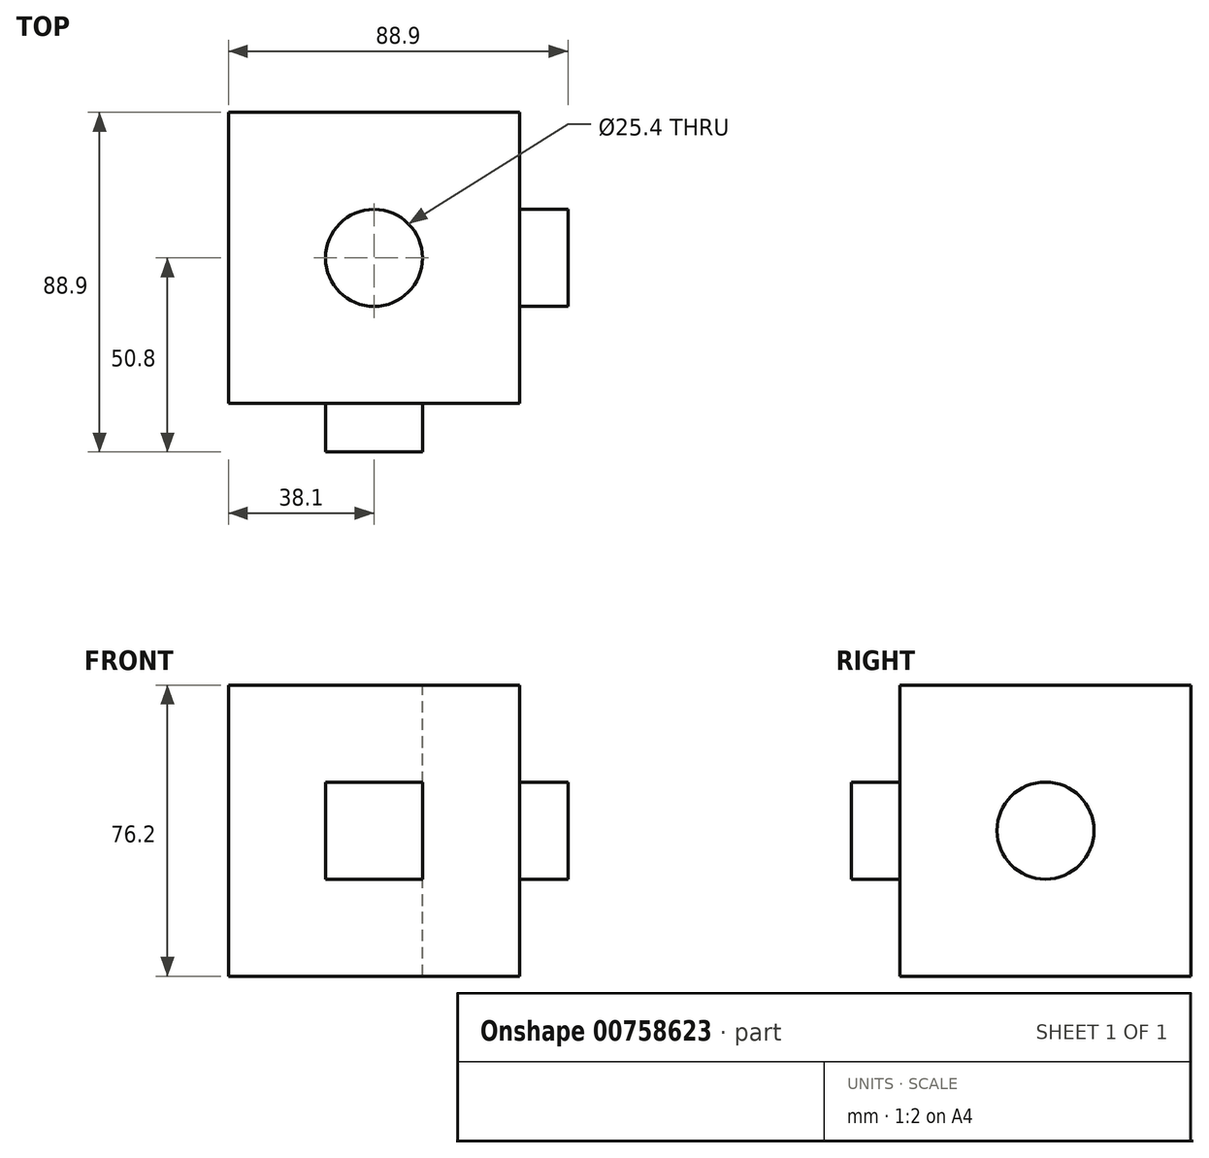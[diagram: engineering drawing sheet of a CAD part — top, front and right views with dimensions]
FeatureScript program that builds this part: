
annotation { "Feature Type Name" : "Feature", "Feature Type Description" : "" }
export const myFeature = defineFeature(function(context is Context, id is Id, definition is map)
    precondition{}
    {
        {
            var Q0;
            Q0=qCreatedBy(makeId("Front.planeOp"),FACE);
            var sketch = newSketch(context, id + "F0", { "sketchPlane" : qUnion([Q0])});
            skLineSegment(sketch, "E0.bottom", {"start": v(-76.2, 55.6) * mm, "end": v(0, 55.6) * mm});
            skLineSegment(sketch, "E0.top", {"start": v(-76.2, -20.6) * mm, "end": v(0, -20.6) * mm});
            skLineSegment(sketch, "E0.left", {"start": v(-76.2, 55.6) * mm, "end": v(-76.2, -20.6) * mm});
            skLineSegment(sketch, "E0.right", {"start": v(0, 55.6) * mm, "end": v(0, -20.6) * mm});
            skSolve(sketch);
        }
        {
            var Q0;
            Q0=makeQuery(id+"F0.imprint","IMPRINT",FACE,{"disambiguationData":[TD([[makeQuery(id+"F0.imprint","IMPRINT",EDGE,{"derivedFrom":sQuery(id+"F0.wireOp",EDGE,"E0.bottom")}),-1.0]])]});
            extrude(context, id + "F1", {"entities" : qUnion([Q0]), "depth" : 76.2 * mm, "offsetDistance" : 25.4 * mm});
        }
        {
            var Q0;
            Q0=makeQuery(id+"F1.opExtrude","CAP_FACE",FACE,{"disambiguationData":[OSD([sQuery(id+"F0.wireOp",EDGE,"E0.bottom"),sQuery(id+"F0.wireOp",EDGE,"E0.top"),sQuery(id+"F0.wireOp",EDGE,"E0.left"),sQuery(id+"F0.wireOp",EDGE,"E0.right")])],"isStart":false});
            var sketch = newSketch(context, id + "F2", { "sketchPlane" : qUnion([Q0])});
            skLineSegment(sketch, "E1.bottom", {"start": v(-50.8, 30.2) * mm, "end": v(-25.4, 30.2) * mm});
            skLineSegment(sketch, "E1.top", {"start": v(-50.8, 4.8) * mm, "end": v(-25.4, 4.8) * mm});
            skLineSegment(sketch, "E1.left", {"start": v(-50.8, 30.2) * mm, "end": v(-50.8, 4.8) * mm});
            skLineSegment(sketch, "E1.right", {"start": v(-25.4, 30.2) * mm, "end": v(-25.4, 4.8) * mm});
            skSolve(sketch);
        }
        {
            var Q0;
            Q0=makeQuery(id+"F2.imprint","IMPRINT",FACE,{"disambiguationData":[TD([[makeQuery(id+"F2.imprint","IMPRINT",EDGE,{"derivedFrom":sQuery(id+"F2.wireOp",EDGE,"E1.bottom")}),-1.0]])]});
            extrude(context, id + "F3", {"entities" : qUnion([Q0]), "operationType" : NewBodyOperationType.ADD, "depth" : 12.7 * mm, "offsetDistance" : 25.4 * mm});
        }
        {
            var Q0;
            Q0=makeQuery(id+"F1.opExtrude","SWEPT_FACE",FACE,{"disambiguationData":[OSD([sQuery(id+"F0.wireOp",EDGE,"E0.right")])]});
            var sketch = newSketch(context, id + "F4", { "sketchPlane" : qUnion([Q0])});
            skCircle(sketch, "E2", {"center": v(-76.2, 16.4) * mm, "radius": 327.7 * mm});
            skCircle(sketch, "E3", {"center": v(-38.1, 17.5) * mm, "radius": 12.7 * mm});
            skSolve(sketch);
        }
        {
            var Q0;
            Q0=makeQuery(id+"F4.imprint","IMPRINT",FACE,{"disambiguationData":[TD([[makeQuery(id+"F4.imprint","IMPRINT",EDGE,{"derivedFrom":sQuery(id+"F4.wireOp",EDGE,"E3")}),1.0]])]});
            extrude(context, id + "F5", {"entities" : qUnion([Q0]), "operationType" : NewBodyOperationType.ADD, "depth" : 12.7 * mm, "offsetDistance" : 25.4 * mm});
        }
        {
            var Q0;
            Q0=makeQuery(id+"F1.opExtrude","SWEPT_FACE",FACE,{"disambiguationData":[OSD([sQuery(id+"F0.wireOp",EDGE,"E0.bottom")])]});
            var sketch = newSketch(context, id + "F6", { "sketchPlane" : qUnion([Q0])});
            skPoint(sketch, "E4", {"position": v(-38.1, -38.1) * mm});
            skSolve(sketch);
        }
        {
            var Q0;
            Q0=sQuery(id+"F6.wireOp",VERTEX,"E4");
            var Q1;
            Q1=makeQuery(id+"F1.opExtrude","SWEPT_BODY",BODY,{"disambiguationData":[OSD([sQuery(id+"F0.wireOp",EDGE,"E0.bottom"),sQuery(id+"F0.wireOp",EDGE,"E0.top"),sQuery(id+"F0.wireOp",EDGE,"E0.left"),sQuery(id+"F0.wireOp",EDGE,"E0.right")])]});
            hole(context, id + "F7", {"style" : HoleStyle.SIMPLE, "endStyle" : HoleEndStyle.THROUGH, "holeDiameter" : 25.4 * mm, "majorDiameter" : 6.35 * mm, "isTappedThrough" : true, "tappedDepth" : 12.7 * mm, "tapClearance" : 3, "locations" : qUnion([Q0]), "scope" : qUnion([Q1])});
        }
    });
